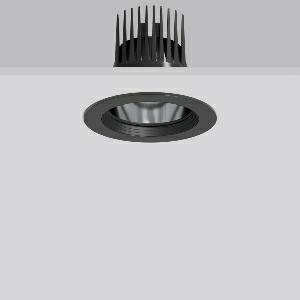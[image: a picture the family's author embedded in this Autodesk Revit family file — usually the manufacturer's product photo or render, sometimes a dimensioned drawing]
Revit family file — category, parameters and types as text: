
# Revit family: heledon_maxi_e_901758_003_3_60ad
name_source: partatom
category: Lighting Fixtures
units: mm (PartAtom-declared; Revit-internal decimal feet)

## family parameters
Cut with Voids When Loaded = No
Host = Face
Light Source = No
Part Type = Normal
Room Calculation Point = No
Round Connector Dimension = Use Diameter
Shared = No

## types (1)
- HELEDON maxi E (1 x LED Modul 935, 3400 lm, 3500)
    Apparent Load = 25 VA
    Approval mark = CE
    CIE Flux Codes = 100 100 100 100 100
    Color Rendering = 92
    Color Temperature = 3500
    Default Elevation = 1800 mm
    Description = Series: HELEDON maxi
Round recessed downlight. Housing: die-cast aluminium, powder-coated. Black plastic ring and recessed LED to prevent glare from the side. Optical assembly with reflector made of MIRO-Silver with 98% total light reflection for outstanding efficiency - can be changed without tools. Best colour rendering index Ra>90. Suitable for Recessed ceiling mounting. Installation without tools thanks to spring fastening system. Including separate LED converter with connecting cable 600 mm.High quality converter without flickering and stroboscopic effect. Through-wiring box (5 pole) available as accessory. The following accessories can be mounted without use of tools: interchangeable lenses, decorative glasses, honeycomb louvre, clear and frosted diffusers, white interchangeable plastic ring. 
Colour: deep black, matt (RAL 9005)
Diameter: 162 mm
Height: 3 mm
Cut-out diameter: 152 mm
Recess height: 200 mm
Luminaire: recess height: 135 mm
Lamp: LED
Socket: without socket
Colour temperature: 3500K
Colour rendering index (CRI): 92
System power: 25 W
Rated luminous flux: 3400 lm
Luminous efficiency: 136 lm/W
Control gear: Regulated power supply
Protection class: II
Type of protection: IP 20
    Height = 0 mm  [stored 0 ft]
    Lamp = 1 x LED Modul 935
    Lamp Light Flux = 3400 lm
    Lamp count = 1
    Length = 162 mm
    Lifetime = 50000 h
    Luminous efficacy = 136 lm/W
    Manufacturer = RZB
    ModVariant = No
    Model = 901758.003.3
    Mounting Place = Ceiling
    Mounting Type = Recessed
    Number of Poles = 1
    OnlyDefault = Yes
    Power Factor = 1
    Product Name = HELEDON maxi E
    Product group = Recessed downlights
    ProductGroupID = 402
    Protection Class = Protection class II
    Protection Degree = IP 20
    RLX_Detail_Level = 1
    RLX_Emergency_Light_Flux = 0 lm
    RLX_Emergency_Type = 0
    RLX_Emergency_Type_DB = No
    RlxData = <blob elided: 122349 chars, md5=a1ad8a7e>
    Socket = socket
    Standby Power = 0 W
    System Light Flux = 3400 lm
    System Power = 25 W
    Type Comments = Product without accessories
    Type Image = 901662.003.jpg
    URL = http://relux.com
    VarID = ---
    Voltage = 230 V
    Voltage Range = 220-240 V
    Weight = 0.00 kg
    Width = 0 mm  [stored 0 ft]

note: [stored X ft] marks values corroborated as IEEE doubles in the binary element streams (Revit-internal decimal feet)

## geometry (parser evidence)
native form markers: Blend x4, Sweep x12
no freeform markers — native parametric forms only
